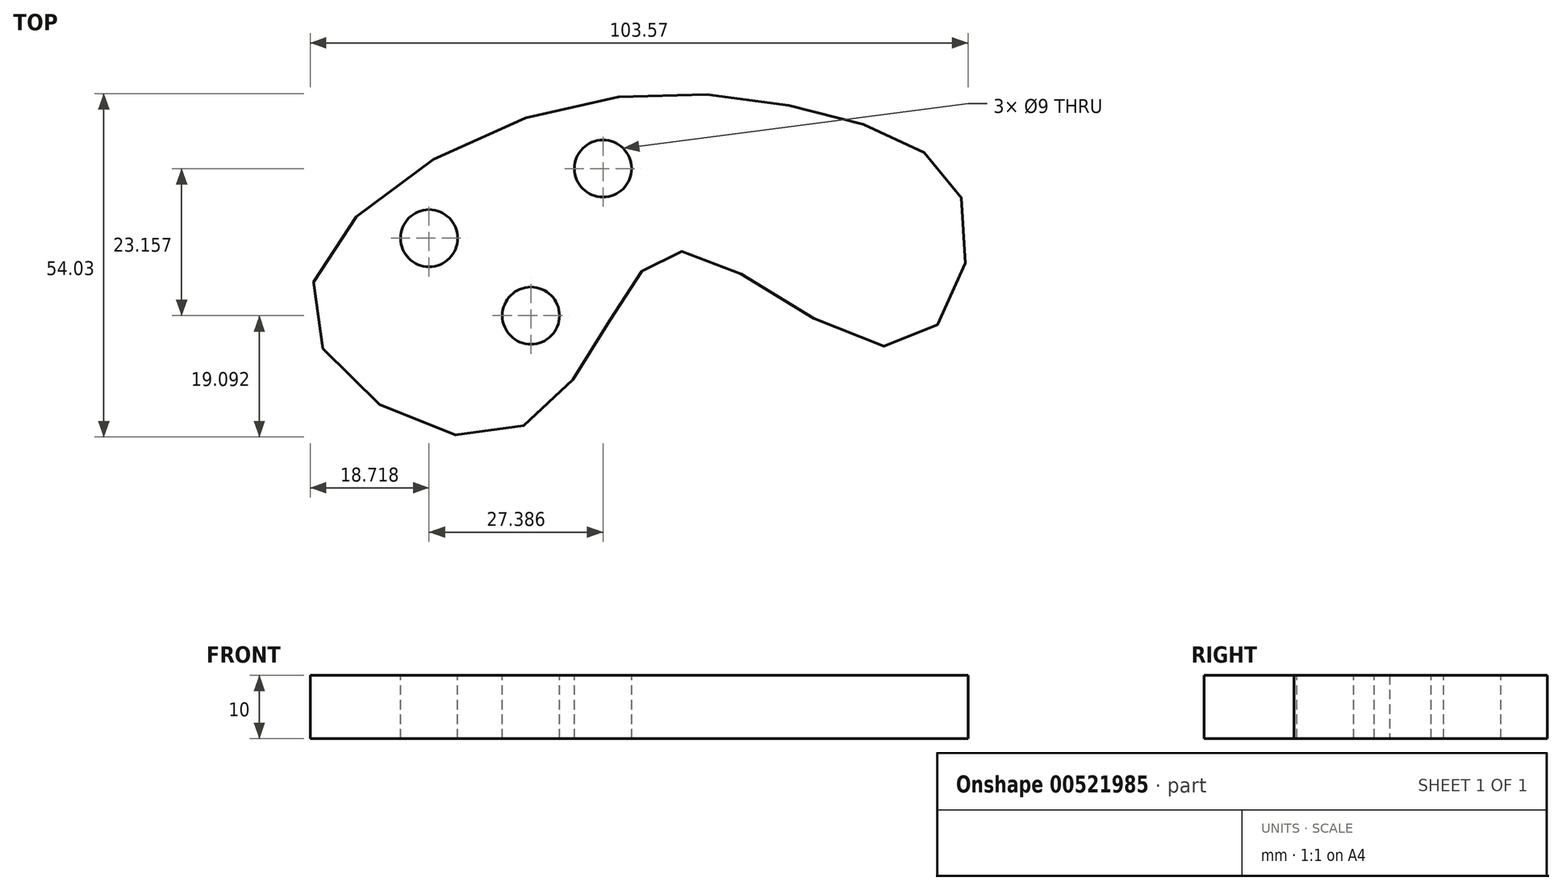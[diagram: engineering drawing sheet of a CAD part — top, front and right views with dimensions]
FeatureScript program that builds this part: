
annotation { "Feature Type Name" : "Feature", "Feature Type Description" : "" }
export const myFeature = defineFeature(function(context is Context, id is Id, definition is map)
    precondition{}
    {
        {
            var Q0;
            Q0=qCreatedBy(makeId("Top.planeOp"),FACE);
            var sketch = newSketch(context, id + "F0", { "sketchPlane" : qUnion([Q0])});
            skFitSpline(sketch, "E0", {"points": [v(-26.25, 21.24) * mm, v(22.1, 21.59) * mm, v(42.83, 7.08) * mm, v(33.16, -14.68) * mm, v(0, 0) * mm, v(-11.74, -8.46) * mm, v(-31.43, -28.84) * mm, v(-60.1, -9.84) * mm, v(-26.25, 21.24) * mm]});
            skSolve(sketch);
        }
        {
            var Q0;
            Q0 = qSketchRegion(id + "F0", true);
            extrude(context, id + "F1", {"entities" : qUnion([Q0]), "depth" : 10 * mm, "offsetDistance" : 25 * mm});
        }
        {
            var Q0;
            Q0=makeQuery(id+"F1.opExtrude","CAP_FACE",FACE,{"disambiguationData":[OSD([sQuery(id+"F0.wireOp",EDGE,"E0")])],"isStart":false});
            var sketch = newSketch(context, id + "F2", { "sketchPlane" : qUnion([Q0])});
            skPoint(sketch, "E1", {"position": v(-41.5, 2.27) * mm});
            skPoint(sketch, "E2", {"position": v(-14.1, 13.24) * mm});
            skPoint(sketch, "E3", {"position": v(-25.46, -9.92) * mm});
            skSolve(sketch);
        }
        {
            var Q0;
            Q0=sQuery(id+"F2.wireOp",VERTEX,"E1");
            var Q1;
            Q1=sQuery(id+"F2.wireOp",VERTEX,"E3");
            var Q2;
            Q2=sQuery(id+"F2.wireOp",VERTEX,"E2");
            var Q3;
            Q3=makeQuery(id+"F1.opExtrude","SWEPT_BODY",BODY,{"disambiguationData":[OSD([sQuery(id+"F0.wireOp",EDGE,"E0")])]});
            hole(context, id + "F3", {"style" : HoleStyle.SIMPLE, "endStyle" : HoleEndStyle.THROUGH, "standardTappedOrClearance" : lookupTablePath({ "fit" : "Normal", "standard" : "ISO", "size" : "M8", "type" : "Clearance" }), "standardBlindInLast" : lookupTablePath({ "fit" : "Normal", "standard" : "ISO", "engagement" : "75%", "pitch" : "1.25 mm", "size" : "M8", "type" : "Clearance & tapped" }), "holeDiameter" : 9 * mm, "majorDiameter" : 5 * mm, "tappedDepth" : 23.1 * mm, "tapClearance" : 3, "locations" : qUnion([Q0, Q1, Q2]), "scope" : qUnion([Q3])});
        }
    });
